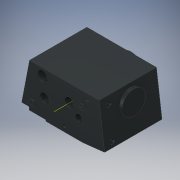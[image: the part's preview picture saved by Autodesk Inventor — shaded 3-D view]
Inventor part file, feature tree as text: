
AUTODESK INVENTOR PART (.ipt)
format: ipt  version: 2018 (Build 220112000, 112)  size: 361,472 bytes
history: native  units: in
note: dims shown in document units (in); Inventor stores cm internally (conversion verified against a paired STEP export)
features: extrude x23, sketch x21, fillet x2, thread x2, plane x2, hole x1, other x1
ambient origin geometry x8: Origin, YZ Plane, XZ Plane, XY Plane, X Axis, Y Axis, Z Axis, Center Point
bodies: Solid1 (feature_tree)
feature tree (52):
  extrude  "Extrusion1"  Depth=10.4921in
  sketch  "Sketch3"  dims[d7=10.0in d8=0.5669in]
  extrude  "Extrusion2"  Depth=0.5669in
  extrude  "Extrusion3"  Depth=0.694in
  extrude  "Extrusion4"  Depth=0.7087in
  extrude  "Extrusion5"  Depth=0.0787in
  extrude  "Extrusion6"  Depth=13.4646in TaperAngle=0.0deg
  fillet  "Fillet1"  Radius=5.5118in
  fillet  "Fillet2"  Radius=6.2992in
  extrude  "Extrusion7"  Depth=2.7559in
  thread  "Thread1"  [1 undecoded]
  extrude  "Extrusion8"  Depth=1.1811in
  plane  "Work Plane3"
  extrude  "Extrusion10"  Depth=1.7717in
  extrude  "Extrusion11"  Depth=1.2106in
  extrude  "Extrusion12"  Depth=2.3622in TaperAngle=0.0deg
  extrude  "Extrusion13"  Depth=1.0236in TaperAngle=0.0deg
  extrude  "Extrusion14"  Depth=1.0236in TaperAngle=0.0deg
  hole  "Hole1"  [1 undecoded]
  extrude  "Extrusion15"  Depth=0.315in
  extrude  "Extrusion16"  Depth=0.0787in
  extrude  "Extrusion17"  Depth=0.7874in
  thread  "Thread2"  [1 undecoded]
  plane  "Work Plane2"
  extrude  "Extrusion18"  Depth=0.3937in
  extrude  "Extrusion19"  Depth=0.3937in TaperAngle=0.0deg
  extrude  "Extrusion20"  Depth=1.1811in
  sketch  "Sketch25"  dims[d97=1.9685in d98=0.0in d103=1.1811in]
  extrude  "Extrusion21"  Depth=0.1969in
  extrude  "Extrusion22"  Depth=0.1969in
  extrude  "Extrusion23"  TaperAngle=90.0deg  [1 undecoded]
  extrude  "Extrusion24"  Depth=2.7559in
  sketch  "Sketch1"  dims[d0=8.6614in d1=10.4921in]
  sketch  "Sketch4"  dims[d9=9.6457in d10=0.694in]
  sketch  "Sketch5"  dims[d11=1.7717in d12=0.7087in]
  sketch  "Sketch6"  dims[d14=16.3386in d15=0.0787in]
  sketch  "Sketch7"  dims[d16=0.0787in d17=13.4646in d18=0.0in d22=5.5118in d26=6.2992in]
  sketch  "Sketch8"  dims[d27=2.7559in d28=3.6024in d29=2.7559in]
  sketch  "Sketch10"  dims[d30=0.3937in d31=0.0in d34=1.1811in]
  sketch  "Sketch12"  dims[d37=1.7717in d38=2.0079in]
  sketch  "Sketch13"  dims[d39=1.2402in d42=1.2106in]
  sketch  "Sketch14"  dims[d43=1.8799in d44=2.3622in d45=0.0in]
  sketch  "Sketch16"  dims[d49=6.3386in d53=1.0236in d54=0.0in]
  sketch  "Sketch17"  dims[d55=2.2835in d56=1.0236in d57=0.0in]
  sketch  "Sketch19"  dims[d69=0.7874in d70=1.378in]
  sketch  "Sketch20"  dims[d72=0.3937in d73=0.315in]
  sketch  "Sketch21"  dims[d75=0.2362in d76=0.0in d77=0.0787in]
  other  "Work Axis1"
  sketch  "Sketch22"  dims[d78=0.0787in d82=0.7874in d83=1.1811in d84=0.0in]
  sketch  "Sketch23"  dims[d85=0.3937in d86=0.0in d87=3.0118in]
  sketch  "Sketch24"  dims[d88=45.0deg d91=0.3937in d92=0.0in]
  sketch  "Sketch26"  dims[d105=0.3937in d106=0.0in d107=5.9055in d108=5.9646in d109=90.0deg d110=2.7559in d111=7.4803in d112=90.0deg d113=0.3937in d114=0.0in d116=0.3937in d117=0.0in d118=2.9528in d120=3.2283in d121=1.1811in d122=0.1969in d123=0.0in d124=0.2559in d125=0.1181in d126=0.2362in d127=0.2559in d128=0.0787in d129=90.0deg d130=0.1969in d131=0.0in d132=6.6929in d133=90.0deg d134=1.7323in d135=2.4409in d136=0.7874in d137=0.0in d138=5.9055in d139=5.9646in d140=90.0deg d141=2.1654in d142=2.7559in d143=0.0in d144=0.9843in d145=1.3386in d146=0.7874in d147=0.7874in d148=0.0in d149=0.3937in d150=0.0in d151=0.0in d152=1.2992in d153=0.0in d154=17.3258in d155=0.0in d156=0.4331in d157=0.0in d160=0.1969in d163=0.1969in d164=0.1969in d165=0.5512in d166=0.0in d167=0.5512in d168=0.0in d169=0.5512in d170=0.0in d171=0.0394in d172=0.0in d173=4.0in d174=5.5118in]
note: 4 required parameter values undecoded (feature->parameter linkage not recoverable at this tier; creation-order binding heuristic only, values carry confidence <= 0.55)
